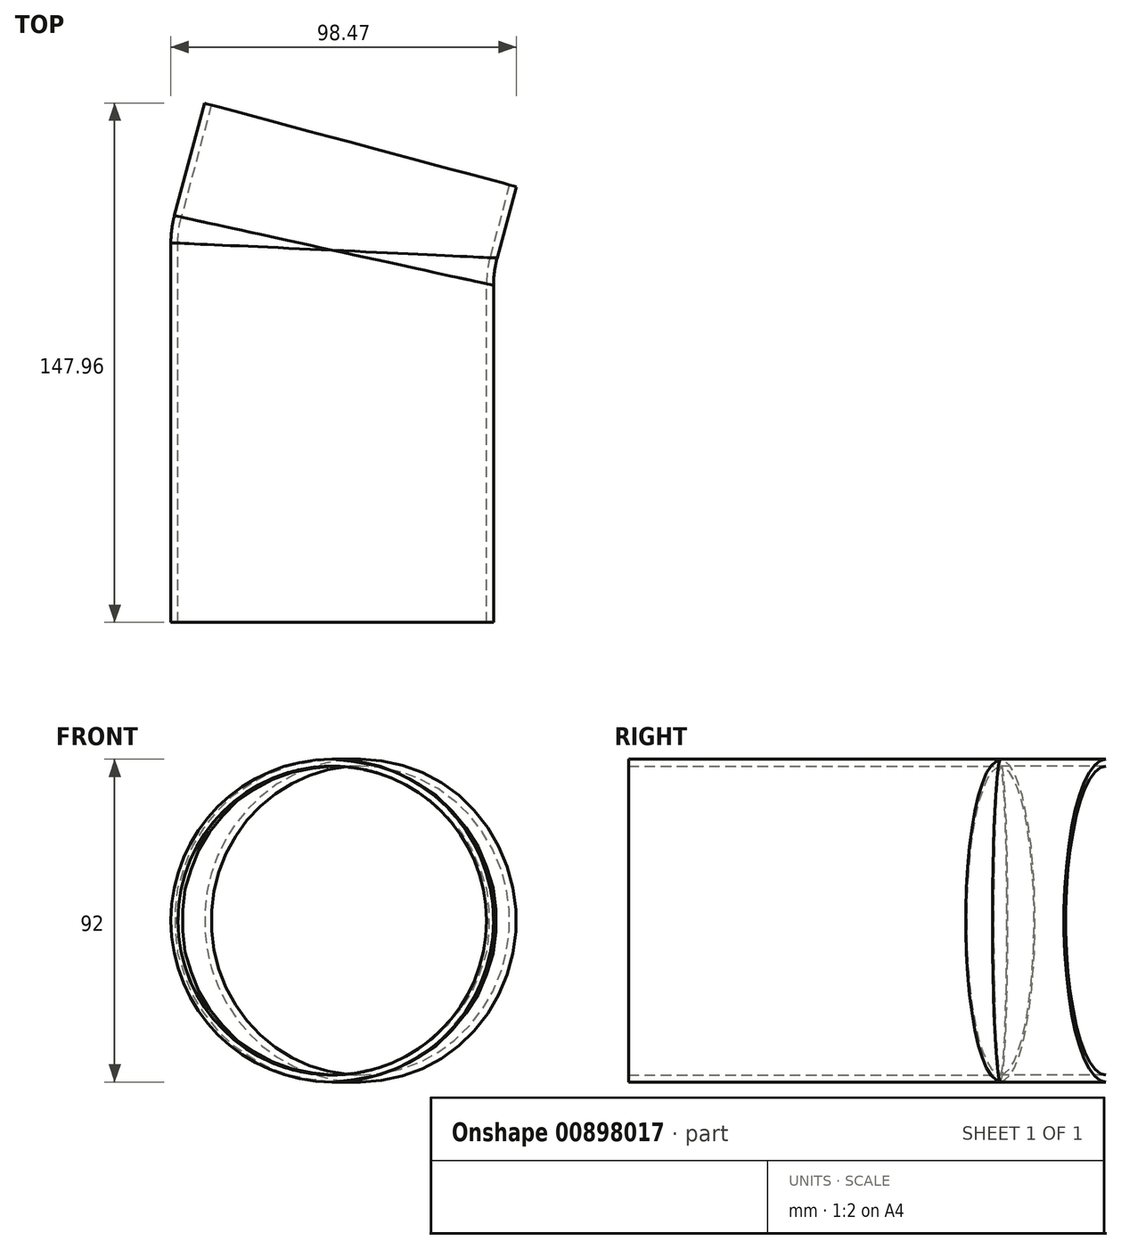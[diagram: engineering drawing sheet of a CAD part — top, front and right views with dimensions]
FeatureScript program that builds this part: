
annotation { "Feature Type Name" : "Feature", "Feature Type Description" : "" }
export const myFeature = defineFeature(function(context is Context, id is Id, definition is map)
    precondition{}
    {
        {
            var Q0;
            Q0=qCreatedBy(makeId("Front.planeOp"),FACE);
            var sketch = newSketch(context, id + "F0", { "sketchPlane" : qUnion([Q0])});
            skCircle(sketch, "E0", {"center": v(0, 0) * mm, "radius": 46 * mm});
            skSolve(sketch);
        }
        {
            var Q0;
            Q0=makeQuery(id+"F0.imprint","IMPRINT",FACE,{"disambiguationData":[TD([[makeQuery(id+"F0.imprint","IMPRINT",EDGE,{"derivedFrom":sQuery(id+"F0.wireOp",EDGE,"E0")}),1.0]])]});
            extrude(context, id + "F1", {"entities" : qUnion([Q0]), "depth" : 50 * mm, "offsetDistance" : 25 * mm});
        }
        {
            var Q0;
            Q0=qCreatedBy(makeId("Top.planeOp"),FACE);
            var sketch = newSketch(context, id + "F2", { "sketchPlane" : qUnion([Q0])});
            skLineSegment(sketch, "E1", {"start": v(0, 0) * mm, "end": v(46, 0) * mm, "construction": true});
            skLineSegment(sketch, "E2", {"start": v(46, 0) * mm, "end": v(-46, 0) * mm});
            skLineSegment(sketch, "E3", {"start": v(-46, 0) * mm, "end": v(-46, -12.89) * mm});
            skLineSegment(sketch, "E4", {"start": v(46, 0) * mm, "end": v(46, -25) * mm});
            skLineSegment(sketch, "E5", {"start": v(46, -25) * mm, "end": v(-46, -12.89) * mm});
            skSolve(sketch);
        }
        {
            var Q0;
            Q0=qSketchRegion(id+"F2",true);
            extrude(context, id + "F3", {"entities" : qUnion([Q0]), "operationType" : NewBodyOperationType.REMOVE, "endBound" : BoundingType.THROUGH_ALL, "oppositeDirection" : true, "depth" : 25 * mm, "offsetDistance" : 25 * mm, "hasSecondDirection" : true, "secondDirectionBound" : SecondDirectionBoundingType.THROUGH_ALL, "secondDirectionOppositeDirection" : false, "secondDirectionDepth" : 25 * mm});
        }
        {
            var Q0;
            Q0=qCreatedBy(makeId("Front.planeOp"),FACE);
            var sketch = newSketch(context, id + "F4", { "sketchPlane" : qUnion([Q0])});
            skCircle(sketch, "E6", {"center": v(0, 0) * mm, "radius": 44 * mm});
            skSolve(sketch);
        }
        {
            var Q0;
            Q0=qSketchRegion(id+"F4",true);
            extrude(context, id + "F5", {"entities" : qUnion([Q0]), "operationType" : NewBodyOperationType.REMOVE, "endBound" : BoundingType.THROUGH_ALL, "depth" : 25 * mm, "offsetDistance" : 25 * mm});
        }
        {
            var Q0;
            Q0=makeQuery(id+"F1.opExtrude","SWEPT_BODY",BODY,{"disambiguationData":[OSD([sQuery(id+"F0.wireOp",EDGE,"E0")])]});
            var Q1;
            Q1=makeQuery(id+"F3.boolean.opBoolean","COPY",FACE,{"derivedFrom":makeQuery(id+"F3.opExtrude","SWEPT_FACE",FACE,{"disambiguationData":[OSD([sQuery(id+"F2.wireOp",EDGE,"E5")])]})});
            mirror(context, id + "F6", {"operationType" : NewBodyOperationType.ADD, "entities" : qUnion([Q0]), "mirrorPlane" : qUnion([Q1])});
        }
        {
            var Q0;
            {var subQ0=makeQuery(id+"F5.boolean.opBoolean","INTERSECT",EDGE,{"derivedFrom":[makeQuery(id+"F3.boolean.opBoolean","COPY",FACE,{"derivedFrom":makeQuery(id+"F3.opExtrude","SWEPT_FACE",FACE,{"disambiguationData":[OSD([sQuery(id+"F2.wireOp",EDGE,"E5")])]})}),makeQuery(id+"F5.opExtrude","SWEPT_FACE",FACE,{"disambiguationData":[OSD([sQuery(id+"F4.wireOp",EDGE,"E6")])]})]});Q0=makeQuery(id+"F6.boolean.opBoolean","MERGE",EDGE,{"derivedFrom":[subQ0,makeQuery(id+"F6.opPattern","COPY",EDGE,{"derivedFrom":subQ0,"instanceName":"1"})]});}
            var Q1;
            {var subQ0=makeQuery(id+"F3.boolean.opBoolean","INTERSECT",EDGE,{"derivedFrom":[makeQuery(id+"F1.opExtrude","SWEPT_FACE",FACE,{"disambiguationData":[OSD([sQuery(id+"F0.wireOp",EDGE,"E0")])]}),makeQuery(id+"F3.opExtrude","SWEPT_FACE",FACE,{"disambiguationData":[OSD([sQuery(id+"F2.wireOp",EDGE,"E5")])]})]});Q1=makeQuery(id+"F6.boolean.opBoolean","MERGE",EDGE,{"derivedFrom":[subQ0,makeQuery(id+"F6.opPattern","COPY",EDGE,{"derivedFrom":subQ0,"instanceName":"1"})]});}
            fillet(context, id + "F7", {"entities" : qUnion([Q0, Q1]), "radius" : 30 * mm, "tangentPropagation" : true, "allowEdgeOverflow" : false});
        }
        {
            var Q0;
            Q0=makeQuery(id+"F1.opExtrude","CAP_FACE",FACE,{"disambiguationData":[OSD([sQuery(id+"F0.wireOp",EDGE,"E0")])],"isStart":false});
            var sketch = newSketch(context, id + "F8", { "sketchPlane" : qUnion([Q0])});
            skCircle(sketch, "E7", {"center": v(0, 0) * mm, "radius": 46 * mm});
            skCircle(sketch, "E8", {"center": v(0, 0) * mm, "radius": 44 * mm});
            skSolve(sketch);
        }
        {
            var Q0;
            Q0 = qSketchRegion(id + "F8", true);
            extrude(context, id + "F9", {"entities" : qUnion([Q0]), "operationType" : NewBodyOperationType.ADD, "depth" : 75 * mm, "offsetDistance" : 25 * mm});
        }
    });
